# Revit family: ВКПД
name_source: partatom
category: Оборудование
units: mm (PartAtom-declared; Revit-internal decimal feet)

## family parameters
Всегда вертикально = Да
Классификация = Нет
На основе рабочей плоскости = Нет
Общий = Нет
При загрузке вырезать с полостями = Нет
Размер круглого соединителя = Использовать диаметр
Тип детали = Нормальный
Точка принадлежности помещению = Нет

## types (31) — shared parameters
00_20_Manufacturer = Вентс
00_20_Name = Вентилятор канальний димовидалення
Casing Material = Металл, окрашенный, синий, матовый RAL 5007
Grid Material = Cover Grid Cross
Load Classification = HVAC
Maintenance zone material = <По категории>
Струм = 0 А
zero-valued in all types: Отметка по умолчанию

## per-type parameters (varying)
| type | A | A1 | A2 | B | B1 | B2 | C | D | D1 | D2 | H | Hole | Maximum Air Flow | Number of Fase | Power | Voltage | b | b1 | c | r | Вага | Двигатель |
| ВКПД-250-2E/0,37-500х300 | 500 мм | 520 мм | 540 мм | 300 мм | 320 мм | 340 мм | 680 мм | 200 мм | 160 мм | 120 мм | 557 мм | Нет | 640.0 л/с | 1 | 370 Вт | 230 В | 135 мм | 100 мм | 322 мм | 17 мм | 40.00 кг | Двигатель : Двигатель_250 |
| ВКПД-710-4Д/7,5-1200x900 | 1200 мм | 1220 мм | 1245 мм | 900 мм | 920 мм | 945 мм | 1040 мм | 480 мм | 384 мм | 288 мм | 1354 мм | Да | 7700.0 л/с | 3 | 7500 Вт | 400 В | 405 мм | 300 мм | 466 мм | 40 мм | 178.00 кг | Двигатель : Двигатель_710 |
| ВКПД-280-2E/0,55-600x300 | 600 мм | 620 мм | 640 мм | 300 мм | 320 мм | 340 мм | 680 мм | 240 мм | 192 мм | 144 мм | 558 мм | Нет | 875.0 л/с | 1 | 550 Вт | 230 В | 135 мм | 100 мм | 322 мм | 20 мм | 40.00 кг | Двигатель : Двигатель_280 |
| ВКПД-315-2E/1,1-600x350 | 600 мм | 620 мм | 640 мм | 350 мм | 370 мм | 390 мм | 680 мм | 240 мм | 192 мм | 144 мм | 624 мм | Нет | 1280.0 л/с | 1 | 1100 Вт | 230 В | 158 мм | 117 мм | 322 мм | 20 мм | 56.00 кг | Двигатель : Двигатель_315 |
| ВКПД-355-4E/0,37-700x400 | 700 мм | 720 мм | 740 мм | 400 мм | 420 мм | 440 мм | 680 мм | 280 мм | 224 мм | 168 мм | 657 мм | Да | 915.0 л/с | 1 | 370 Вт | 230 В | 180 мм | 133 мм | 322 мм | 23 мм | 51.00 кг | Двигатель : Двигатель_280 |
| ВКПД-400-4E/0,55-700x500 | 700 мм | 720 мм | 740 мм | 500 мм | 520 мм | 540 мм | 680 мм | 280 мм | 224 мм | 168 мм | 772 мм | Да | 1250.0 л/с | 1 | 550 Вт | 230 В | 225 мм | 167 мм | 322 мм | 23 мм | 70.00 кг | Двигатель : Двигатель_400 |
| ВКПД-450-4E/0,75-800х600 | 800 мм | 820 мм | 840 мм | 600 мм | 620 мм | 640 мм | 800 мм | 320 мм | 256 мм | 192 мм | 872 мм | Да | 1880.0 л/с | 1 | 750 Вт | 230 В | 270 мм | 200 мм | 370 мм | 27 мм | 89.00 кг | Двигатель : Двигатель_450 |
| ВКПД-500-4E/1,5-800х600 | 800 мм | 820 мм | 840 мм | 600 мм | 620 мм | 640 мм | 840 мм | 320 мм | 256 мм | 192 мм | 914 мм | Да | 2700.0 л/с | 1 | 1500 Вт | 230 В | 270 мм | 200 мм | 386 мм | 27 мм | 97.00 кг | Двигатель : Двигатель_500 |
| ВКПД-560-4E/3-900х700 | 900 мм | 920 мм | 940 мм | 700 мм | 720 мм | 740 мм | 840 мм | 360 мм | 288 мм | 216 мм | 1058 мм | Да | 3800.0 л/с | 1 | 3000 Вт | 230 В | 315 мм | 233 мм | 386 мм | 30 мм | 100.00 кг | Двигатель : Двигатель_560 |
| ВКПД-630-4Д/4-1000х800 | 1000 мм | 1020 мм | 1040 мм | 800 мм | 820 мм | 840 мм | 1040 мм | 400 мм | 320 мм | 240 мм | 1150 мм | Да | 5150.0 л/с | 3 | 4000 Вт | 400 В | 360 мм | 267 мм | 466 мм | 33 мм | 130.00 кг | Двигатель : Двигатель_630 |
| ВКПД-250-2Д/0,37-500х300 | 500 мм | 520 мм | 540 мм | 300 мм | 320 мм | 340 мм | 680 мм | 200 мм | 160 мм | 120 мм | 557 мм | Нет | 640.0 л/с | 3 | 370 Вт | 400 В | 135 мм | 100 мм | 322 мм | 17 мм | 40.00 кг | Двигатель : Двигатель_250 |
| ВКПД-250-2/4Д/0,37/0,1-500х300 | 500 мм | 520 мм | 540 мм | 300 мм | 320 мм | 340 мм | 680 мм | 200 мм | 160 мм | 120 мм | 557 мм | Нет | 640.0 л/с | 3 | 370 Вт | 400 В | 135 мм | 100 мм | 322 мм | 17 мм | 40.00 кг | Двигатель : Двигатель_250 |
| ВКПД-280-2Д/0,55-600x300 | 600 мм | 620 мм | 640 мм | 300 мм | 320 мм | 340 мм | 680 мм | 240 мм | 192 мм | 144 мм | 558 мм | Нет | 875.0 л/с | 3 | 550 Вт | 400 В | 135 мм | 100 мм | 322 мм | 20 мм | 40.00 кг | Двигатель : Двигатель_280 |
| ВКПД-280-2/4Д/0,55/0,1-600x300 | 600 мм | 620 мм | 640 мм | 300 мм | 320 мм | 340 мм | 680 мм | 240 мм | 192 мм | 144 мм | 558 мм | Нет | 875.0 л/с | 3 | 550 Вт | 400 В | 135 мм | 100 мм | 322 мм | 20 мм | 40.00 кг | Двигатель : Двигатель_280 |
| ВКПД-315-2Д/1,1-600x350 | 600 мм | 620 мм | 640 мм | 350 мм | 370 мм | 390 мм | 680 мм | 240 мм | 192 мм | 144 мм | 624 мм | Нет | 1280.0 л/с | 3 | 1100 Вт | 400 В | 158 мм | 117 мм | 322 мм | 20 мм | 56.00 кг | Двигатель : Двигатель_315 |
| ВКПД-315-2/4Д/1,1/0,25-600x350 | 600 мм | 620 мм | 640 мм | 350 мм | 370 мм | 390 мм | 680 мм | 240 мм | 192 мм | 144 мм | 624 мм | Нет | 1280.0 л/с | 3 | 1100 Вт | 400 В | 158 мм | 117 мм | 322 мм | 20 мм | 56.00 кг | Двигатель : Двигатель_315 |
| ВКПД-355-4Д/0,37-700x400 | 700 мм | 720 мм | 740 мм | 400 мм | 420 мм | 440 мм | 680 мм | 280 мм | 224 мм | 168 мм | 657 мм | Да | 915.0 л/с | 3 | 370 Вт | 400 В | 180 мм | 133 мм | 322 мм | 23 мм | 51.00 кг | Двигатель : Двигатель_280 |
| ВКПД-355-4/6Д/0,55/0,1-700x400 | 700 мм | 720 мм | 740 мм | 400 мм | 420 мм | 440 мм | 680 мм | 280 мм | 224 мм | 168 мм | 657 мм | Да | 915.0 л/с | 3 | 550 Вт | 400 В | 180 мм | 133 мм | 322 мм | 23 мм | 51.00 кг | Двигатель : Двигатель_280 |
| ВКПД-400-4Д/0,55-700x500 | 700 мм | 720 мм | 740 мм | 500 мм | 520 мм | 540 мм | 680 мм | 280 мм | 224 мм | 168 мм | 772 мм | Да | 1250.0 л/с | 3 | 550 Вт | 400 В | 225 мм | 167 мм | 322 мм | 23 мм | 70.00 кг | Двигатель : Двигатель_400 |
| ВКПД-400-4/6Д/0,55/0,25-700x500 | 700 мм | 720 мм | 740 мм | 500 мм | 520 мм | 540 мм | 680 мм | 280 мм | 224 мм | 168 мм | 772 мм | Да | 1250.0 л/с | 3 | 550 Вт | 400 В | 225 мм | 167 мм | 322 мм | 23 мм | 70.00 кг | Двигатель : Двигатель_400 |
| ВКПД-450-4Д/0,75-800х600 | 800 мм | 820 мм | 840 мм | 600 мм | 620 мм | 640 мм | 800 мм | 320 мм | 256 мм | 192 мм | 872 мм | Да | 1880.0 л/с | 3 | 750 Вт | 400 В | 270 мм | 200 мм | 370 мм | 27 мм | 89.00 кг | Двигатель : Двигатель_450 |
| ВКПД-450-4/6Д/0,8/0,2-800х600 | 800 мм | 820 мм | 840 мм | 600 мм | 620 мм | 640 мм | 800 мм | 320 мм | 256 мм | 192 мм | 872 мм | Да | 1880.0 л/с | 3 | 800 Вт | 400 В | 270 мм | 200 мм | 370 мм | 27 мм | 89.00 кг | Двигатель : Двигатель_450 |
| ВКПД-500-4Д/1,5-800х600 | 800 мм | 820 мм | 840 мм | 600 мм | 620 мм | 640 мм | 840 мм | 320 мм | 256 мм | 192 мм | 914 мм | Да | 2700.0 л/с | 3 | 1500 Вт | 400 В | 270 мм | 200 мм | 386 мм | 27 мм | 97.00 кг | Двигатель : Двигатель_500 |
| ВКПД-500-4/6Д/1,5/0,37-800х600 | 800 мм | 820 мм | 840 мм | 600 мм | 620 мм | 640 мм | 840 мм | 320 мм | 256 мм | 192 мм | 914 мм | Да | 2700.0 л/с | 3 | 1500 Вт | 400 В | 270 мм | 200 мм | 386 мм | 27 мм | 97.00 кг | Двигатель : Двигатель_500 |
| ВКПД-560-4Д/3-900х700 | 900 мм | 920 мм | 940 мм | 700 мм | 720 мм | 740 мм | 840 мм | 360 мм | 288 мм | 216 мм | 1058 мм | Да | 3800.0 л/с | 3 | 3000 Вт | 400 В | 315 мм | 233 мм | 386 мм | 30 мм | 100.00 кг | Двигатель : Двигатель_560 |
| ВКПД-560-4/6Д/2,8/0,7-900х700 | 900 мм | 920 мм | 940 мм | 700 мм | 720 мм | 740 мм | 840 мм | 360 мм | 288 мм | 216 мм | 1058 мм | Да | 3800.0 л/с | 3 | 2800 Вт | 400 В | 315 мм | 233 мм | 386 мм | 30 мм | 100.00 кг | Двигатель : Двигатель_560 |
| ВКПД-560-4/8Д/2,8/0,55-900x700 | 900 мм | 920 мм | 940 мм | 700 мм | 720 мм | 740 мм | 840 мм | 360 мм | 288 мм | 216 мм | 1058 мм | Да | 3800.0 л/с | 3 | 2800 Вт | 400 В | 315 мм | 233 мм | 386 мм | 30 мм | 100.00 кг | Двигатель : Двигатель_560 |
| ВКПД-630-4/6Д/3,8/1-1000х800 | 1000 мм | 1020 мм | 1040 мм | 800 мм | 820 мм | 840 мм | 1040 мм | 400 мм | 320 мм | 240 мм | 1150 мм | Да | 5150.0 л/с | 3 | 3800 Вт | 400 В | 360 мм | 267 мм | 466 мм | 33 мм | 130.00 кг | Двигатель : Двигатель_630 |
| ВКПД-630-4/8Д/3,8/0,75-1000x800 | 1000 мм | 1020 мм | 1040 мм | 800 мм | 820 мм | 840 мм | 1040 мм | 400 мм | 320 мм | 240 мм | 1150 мм | Да | 5150.0 л/с | 3 | 3800 Вт | 400 В | 360 мм | 267 мм | 466 мм | 33 мм | 130.00 кг | Двигатель : Двигатель_630 |
| ВКПД-710-4/6Д/7,5/2,2-1200x900 | 1200 мм | 1220 мм | 1245 мм | 900 мм | 920 мм | 945 мм | 1040 мм | 480 мм | 384 мм | 288 мм | 1354 мм | Да | 7700.0 л/с | 3 | 7500 Вт | 400 В | 405 мм | 300 мм | 466 мм | 40 мм | 178.00 кг | Двигатель : Двигатель_710 |
| ВКПД-710-4/8Д/7,5/1-1200x900 | 1200 мм | 1220 мм | 1245 мм | 900 мм | 920 мм | 945 мм | 1040 мм | 480 мм | 384 мм | 288 мм | 1354 мм | Да | 7700.0 л/с | 3 | 7500 Вт | 400 В | 405 мм | 300 мм | 466 мм | 40 мм | 178.00 кг | Двигатель : Двигатель_710 |

note: column(s) folded — value = type name in every type: 00_20_Type
